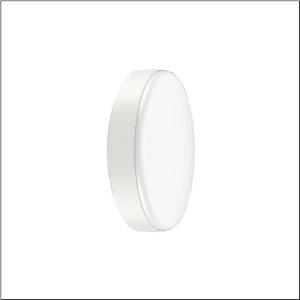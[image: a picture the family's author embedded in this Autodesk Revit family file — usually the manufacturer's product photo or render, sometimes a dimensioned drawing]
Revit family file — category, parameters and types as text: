
# Revit family: rondel_31_51wc10db44as
name_source: partatom
category: Lighting Fixtures
units: mm (PartAtom-declared; Revit-internal decimal feet)

## family parameters
Cut with Voids When Loaded = No
Host = Face
Light Source = No
Part Type = Normal
Room Calculation Point = No
Round Connector Dimension = Use Diameter
Shared = No

## types (1)
- Rondel 31 (1 x LED, 4400 lm, 35.5 W, 4000K)
    Apparent Load = 36 VA
    CIE Flux Codes = 44 75 94 94 100
    Color Rendering = 80
    Color Temperature = 4000K
    Default Elevation = 1800 mm
    Description = Rondel 31, wall and ceiling luminaire, primary optical cover: cover, of PC, opal, light emission: direct distribution, primary light characteristic: symmetric, installation type: surface-mounted, LED, rated luminous flux: 4.400lm, luminous efficacy: 124lm/W, light colour: 840, colour temperature: 4000K, with terminal, 3-pole, max. 2.5mm², mains connection: 220..240V, AC, 50/60Hz, rated input power: 35.5W, luminaire housing, of PC, traffic white (RAL 9016), diameter: 480mm, brightness and presence sensor, HF sensor, protection rating (complete): IP65, insulation class (complete): insulation class II (safety insulation), certification: CE, impact resistance: IK10, permissible operating ambient temperature: -20..+40°C, permissible storage temperature: -20..+60°C, packaging unit: 1 piece
    Height = 97 mm
    Lamp = 1 x LED
    Lamp Light Flux = 4400 lm
    Lamp Power = 35.5 W
    Lamp count = 1
    Length = 480 mm
    Luminous efficacy = 124 lm/W
    Manufacturer = Siteco
    ModVariant = No
    Model = 51WC10DB44AS
    Mounting Place = Ceiling
    Mounting Type = Surface mounted
    Number of Poles = 1
    OnlyDefault = Yes
    Power Factor = 1
    Product Name = Rondel 31
    Product group = wall and ceiling luminaire
    ProductGroupID = 302
    Protection Class = Protection class II
    Protection Degree = IP 65
    RLX_Detail_Level = 1
    RLX_Emergency_Light_Flux = 0 lm
    RLX_Emergency_Type = 0
    RLX_Emergency_Type_DB = No
    RlxData = <blob elided: 40885 chars, md5=d936b5a0>
    Socket = socket
    Standby Power = 0 W
    System Light Flux = 4400 lm
    System Power = 36 W
    Type Comments = Product without accessories
    Type Image = l_1007188.jpg
    URL = http://relux.com
    VarID = ---
    Voltage = 0 V
    Weight = 0.00 kg
    Width = 0 mm  [stored 0 ft]

note: [stored X ft] marks values corroborated as IEEE doubles in the binary element streams (Revit-internal decimal feet)

## geometry (parser evidence)
native form markers: Blend x4, Sweep x12
no freeform markers — native parametric forms only
